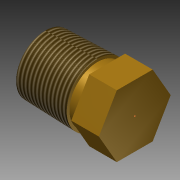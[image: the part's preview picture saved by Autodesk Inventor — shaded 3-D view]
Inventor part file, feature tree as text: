
AUTODESK INVENTOR PART (.ipt)
format: ipt  version: 2011 (Build 150239000, 239)  size: 97,792 bytes
history: native  units: mm (DEFAULTED — no unit token found)
features: thread x2, sketch x1, imported_body x1
ambient origin geometry x8: Origin, YZ Plane, XZ Plane, XY Plane, X Axis, Y Axis, Z Axis, Center Point
bodies: Solid1 (feature_tree)
feature tree (4):
  sketch  "Sketch1"
  imported_body  "Base1"
  thread  "Thread1"  [1 undecoded]
  thread  "Thread2"  [1 undecoded]
note: 2 required parameter values undecoded (feature->parameter linkage not recoverable at this tier; creation-order binding heuristic only, values carry confidence <= 0.55)
